# Revit family: Kanalschienengummi KG
name_source: partatom
category: HLS-Bauteile
units: mm (PartAtom-declared; Revit-internal decimal feet)

## family parameters
Arbeitsebenenbasiert = Ja
Beim Laden mit Abzugskörper schneiden = Nein
Bemaßung runder Anschluss = Durchmesser verwenden
Beschriftungsausrichtung beibehalten = Nein
Gemeinsam genutzt = Ja
Immer vertikal = Nein
Raumberechnungspunkt = Nein
Teiletyp = Normal

## types (6) — shared parameters
Fabrikat = MEFA
Farbe = Schwarz
Gewicht pro Bauteil = 0.00 kg
Gewicht pro Stück = 0.00 kg
Material = Kunststoff
Materialname = TPE
Vorgabe-Ansicht = 1219 mm
max. Temperaturbeständigkeit = 100 °C

## per-type parameters (varying)
| type | Anschluss | Artikelnummer | B | Baustoffklasse | Breite | Dämmstärke | EAN | Gewicht | H | Kurztext1 | Kurztext2 | Länge | Mengeneinheit | Profiltyp | Shore-Härte | vpe |
| Kanalschienengummi KG45 | M10 | 710004502 | 40 mm  [stored 0.131234 ft] |  | 40 mm  [stored 0.131234 ft] | 4 mm  [stored 0.0131234 ft] | 4250928455727 | 0.22 kg | 4 mm  [stored 0.0131234 ft] | Kanalschienengummi C-Profil 45 | 10 m Kunststoff | 10000 mm | m | 45 |  | 10 |
| Kanalschienengummi KG35 | M8 | 710003502 | 28 mm  [stored 0.0918635 ft] |  | 35 mm | 6 mm  [stored 0.019685 ft] | 4250928455710 | 0.17 kg | 4 mm  [stored 0.0131234 ft] | Kanalschienengummi C-Profil 35 | 20 m Kunststoff | 20000 mm | m | 35 |  | 20 |
| Kanalschienengummi KG27/18 | M8 | 710001901 | 22 mm |  | 26 mm | 6 mm  [stored 0.019685 ft] | 4250928459305 | 0.10 kg | 3 mm  [stored 0.00984252 ft] | Kanalschienengummi C-Profil 27 | 20 m Kunststoff | 20000 mm | m | 27/18 |  | 20 |
| Stex Schienengummi 35 | M8 | 1272019 | 35 mm |  | 35 mm | 5 mm  [stored 0.0164042 ft] | 4250928424372 | 0.33 kg | 4 mm  [stored 0.0131234 ft] | Kanalschienengummi C-Profil Stex 35 | 20 m Kunststoff | 20000 mm | m | Stex 35 | 45 Shore | 20 |
| Stex Schienengummi 35, Abschnitt 50 mm | M8 | 1272020 | 35 mm | B2 | 35 mm | 5 mm  [stored 0.0164042 ft] | 4250928424389 | 0.02 kg | 4 mm  [stored 0.0131234 ft] | Schalldämmprofil C-Profil Stex 35 | 50 mm Kunststoff | 50 mm  [stored 0.164042 ft] | St | Stex 35 | 45 Shore | 50 |
| Kanalschienengummi KG45 Abschnitt 100mm | M10 | 710004502/0100 | 40 mm  [stored 0.131234 ft] | B2 | 40 mm  [stored 0.131234 ft] | 4 mm  [stored 0.0131234 ft] | 4250928466662 | 0.02 kg | 4 mm  [stored 0.0131234 ft] | Schalldämmprofil C-Profil  45 | 100 mm Kunststoff | 100 mm  [stored 0.328084 ft] | St | 45 |  | 50 |

note: [stored X ft] marks values corroborated as IEEE doubles in the binary element streams (Revit-internal decimal feet)
